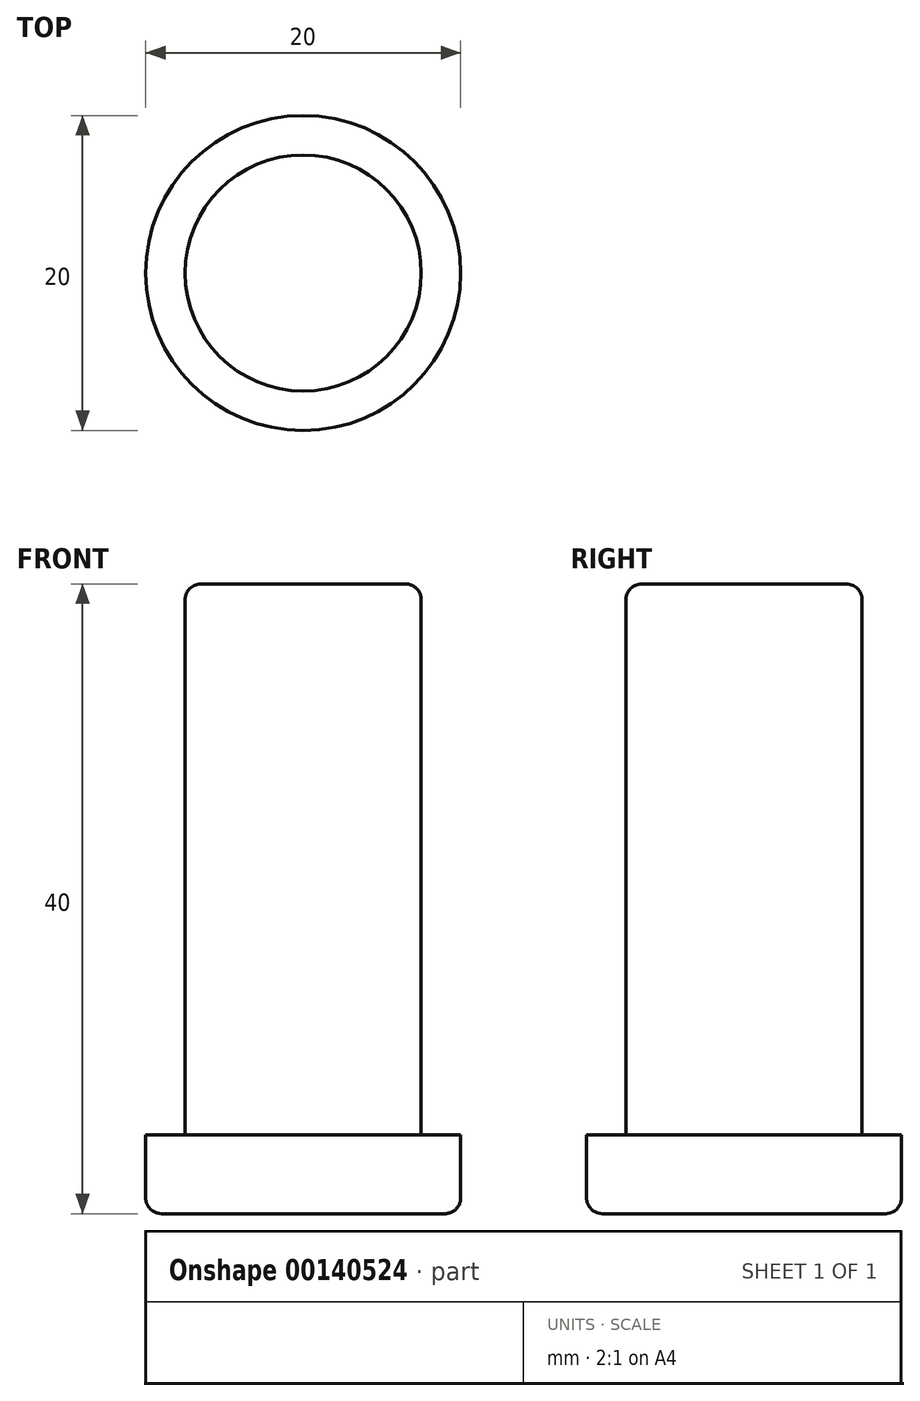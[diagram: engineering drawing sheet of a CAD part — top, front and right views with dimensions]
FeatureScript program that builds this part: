
annotation { "Feature Type Name" : "Feature", "Feature Type Description" : "" }
export const myFeature = defineFeature(function(context is Context, id is Id, definition is map)
    precondition{}
    {
        {
            var Q0;
            Q0=qCreatedBy(makeId("Top.planeOp"),FACE);
            var sketch = newSketch(context, id + "F0", { "sketchPlane" : qUnion([Q0])});
            skCircle(sketch, "E0", {"center": v(0, 0) * mm, "radius": 10 * mm});
            skSolve(sketch);
        }
        {
            var Q0;
            Q0 = qSketchRegion(id + "F0", true);
            extrude(context, id + "F1", {"entities" : qUnion([Q0]), "depth" : 5 * mm});
        }
        {
            var Q0;
            Q0=makeQuery(id+"F1.opExtrude","CAP_FACE",FACE,{"disambiguationData":[OSD([sQuery(id+"F0.wireOp",EDGE,"E0")])],"isStart":false});
            var sketch = newSketch(context, id + "F2", { "sketchPlane" : qUnion([Q0])});
            skCircle(sketch, "E1", {"center": v(0, 0) * mm, "radius": 7.5 * mm});
            skSolve(sketch);
        }
        {
            var Q0;
            Q0 = qSketchRegion(id + "F2", true);
            extrude(context, id + "F3", {"entities" : qUnion([Q0]), "operationType" : NewBodyOperationType.ADD, "depth" : 35 * mm});
        }
        {
            var Q0;
            Q0=makeQuery(id+"F3.opExtrude","CAP_EDGE",EDGE,{"disambiguationData":[OSD([sQuery(id+"F2.wireOp",EDGE,"E1")])],"isStart":false});
            fillet(context, id + "F4", {"entities" : qUnion([Q0]), "radius" : 1 * mm, "tangentPropagation" : true, "allowEdgeOverflow" : false});
        }
        {
            var Q0;
            Q0=makeQuery(id+"F1.opExtrude","CAP_EDGE",EDGE,{"disambiguationData":[OSD([sQuery(id+"F0.wireOp",EDGE,"E0")])],"isStart":true});
            fillet(context, id + "F5", {"entities" : qUnion([Q0]), "radius" : 1 * mm, "tangentPropagation" : true, "allowEdgeOverflow" : false});
        }
    });
